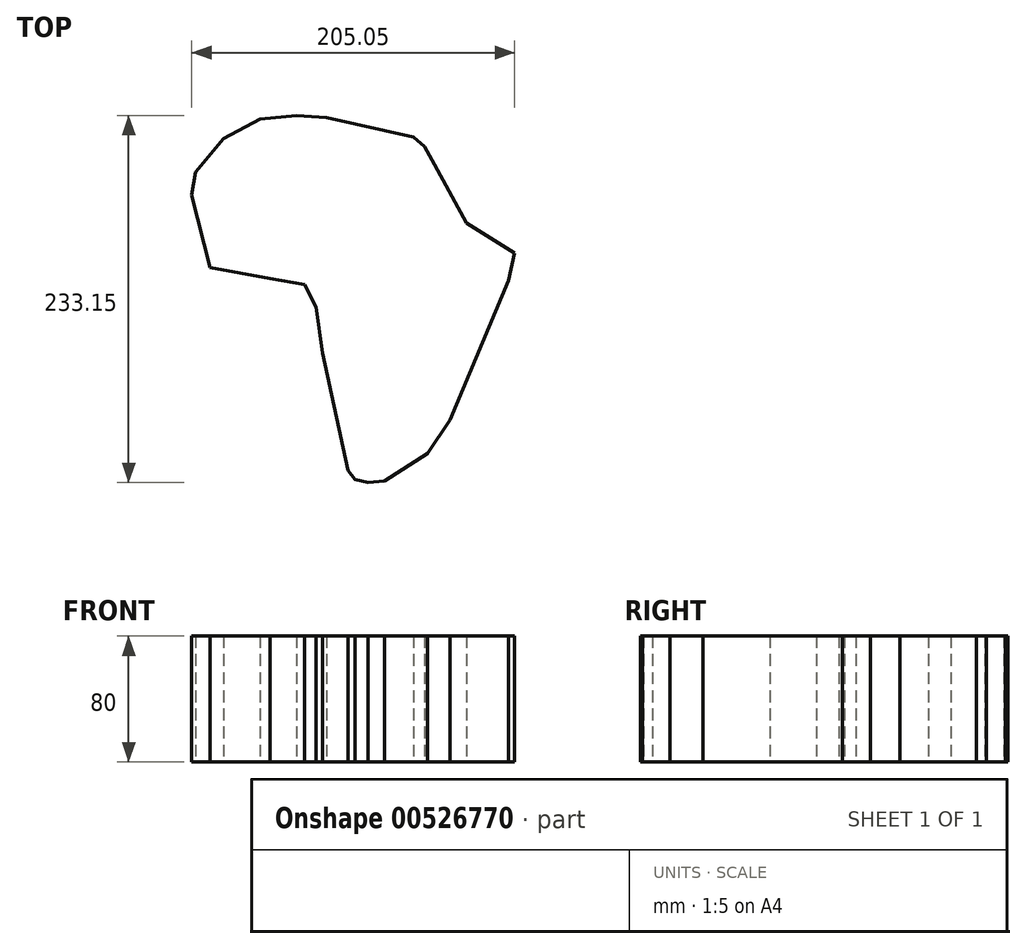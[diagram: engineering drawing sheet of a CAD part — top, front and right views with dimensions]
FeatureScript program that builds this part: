
annotation { "Feature Type Name" : "Feature", "Feature Type Description" : "" }
export const myFeature = defineFeature(function(context is Context, id is Id, definition is map)
    precondition{}
    {
        {
            var Q0;
            Q0=qCreatedBy(makeId("Top.planeOp"),FACE);
            var sketch = newSketch(context, id + "F0", { "sketchPlane" : qUnion([Q0])});
            skLineSegment(sketch, "E0", {"start": v(-465.72, -27.87) * mm, "end": v(-465.72, 203.52) * mm});
            skLineSegment(sketch, "E1", {"start": v(-465.72, 203.52) * mm, "end": v(34.28, 203.52) * mm});
            skLineSegment(sketch, "E2", {"start": v(34.28, 203.52) * mm, "end": v(534.28, 203.52) * mm});
            skLineSegment(sketch, "E3", {"start": v(534.28, 203.52) * mm, "end": v(534.28, -27.87) * mm});
            skLineSegment(sketch, "E4", {"start": v(534.28, -27.87) * mm, "end": v(534.28, -259.27) * mm});
            skLineSegment(sketch, "E5", {"start": v(534.28, -259.27) * mm, "end": v(34.28, -259.27) * mm});
            skLineSegment(sketch, "E6", {"start": v(34.28, -259.27) * mm, "end": v(-465.72, -259.27) * mm});
            skLineSegment(sketch, "E7", {"start": v(-465.72, -259.27) * mm, "end": v(-465.72, -27.87) * mm});
            skLineSegment(sketch, "E8", {"start": v(528.39, -27.87) * mm, "end": v(528.39, 197.62) * mm});
            skLineSegment(sketch, "E9", {"start": v(528.39, 197.62) * mm, "end": v(34.28, 197.62) * mm});
            skLineSegment(sketch, "E10", {"start": v(34.28, 197.62) * mm, "end": v(-459.82, 197.62) * mm});
            skLineSegment(sketch, "E11", {"start": v(-459.82, 197.62) * mm, "end": v(-459.82, -27.87) * mm});
            skLineSegment(sketch, "E12", {"start": v(-459.82, -27.87) * mm, "end": v(-459.82, -253.37) * mm});
            skLineSegment(sketch, "E13", {"start": v(-459.82, -253.37) * mm, "end": v(34.28, -253.37) * mm});
            skLineSegment(sketch, "E14", {"start": v(34.28, -253.37) * mm, "end": v(528.39, -253.37) * mm});
            skLineSegment(sketch, "E15", {"start": v(528.39, -253.37) * mm, "end": v(528.39, -27.87) * mm});
            skLineSegment(sketch, "E16", {"start": v(-215.42, -237.03) * mm, "end": v(-218.6, -212.47) * mm});
            skLineSegment(sketch, "E17", {"start": v(-218.6, -212.47) * mm, "end": v(-201.87, -170.47) * mm});
            skLineSegment(sketch, "E18", {"start": v(-201.87, -170.47) * mm, "end": v(-153.34, -90.03) * mm});
            skLineSegment(sketch, "E19", {"start": v(-153.34, -90.03) * mm, "end": v(-154.95, -75.15) * mm});
            skLineSegment(sketch, "E20", {"start": v(-154.95, -75.15) * mm, "end": v(-201.75, -38.97) * mm});
            skLineSegment(sketch, "E21", {"start": v(-201.75, -38.97) * mm, "end": v(-258.28, -21.52) * mm});
            skLineSegment(sketch, "E22", {"start": v(-258.28, -21.52) * mm, "end": v(-275.6, -23.25) * mm});
            skLineSegment(sketch, "E23", {"start": v(-275.6, -23.25) * mm, "end": v(-281.86, -24.56) * mm});
            skLineSegment(sketch, "E24", {"start": v(-281.86, -24.56) * mm, "end": v(-282.6, -27.58) * mm});
            skLineSegment(sketch, "E25", {"start": v(-282.6, -27.58) * mm, "end": v(-284.13, -31.63) * mm});
            skLineSegment(sketch, "E26", {"start": v(-284.13, -31.63) * mm, "end": v(-297, -64.53) * mm});
            skLineSegment(sketch, "E27", {"start": v(-297, -64.53) * mm, "end": v(-292.56, -86.46) * mm});
            skLineSegment(sketch, "E28", {"start": v(-292.56, -86.46) * mm, "end": v(-273.22, -112.2) * mm});
            skLineSegment(sketch, "E29", {"start": v(-273.22, -112.2) * mm, "end": v(-264.94, -121.42) * mm});
            skLineSegment(sketch, "E30", {"start": v(-264.94, -121.42) * mm, "end": v(-261.57, -146.52) * mm});
            skLineSegment(sketch, "E31", {"start": v(-261.57, -146.52) * mm, "end": v(-248.27, -214.7) * mm});
            skLineSegment(sketch, "E32", {"start": v(-248.27, -214.7) * mm, "end": v(-235.22, -230.35) * mm});
            skLineSegment(sketch, "E33", {"start": v(-235.22, -230.35) * mm, "end": v(-214.64, -241.3) * mm});
            skLineSegment(sketch, "E34", {"start": v(-214.64, -241.3) * mm, "end": v(-215.42, -237.03) * mm});
            skLineSegment(sketch, "E35", {"start": v(-215.42, -237.03) * mm, "end": v(-215.42, -237.03) * mm});
            skLineSegment(sketch, "E36", {"start": v(-293.37, -30.58) * mm, "end": v(-289.65, -28.13) * mm});
            skLineSegment(sketch, "E37", {"start": v(-289.65, -28.13) * mm, "end": v(-293.12, -24.82) * mm});
            skLineSegment(sketch, "E38", {"start": v(-293.12, -24.82) * mm, "end": v(-305, -14.19) * mm});
            skLineSegment(sketch, "E39", {"start": v(-305, -14.19) * mm, "end": v(-321.94, 24.08) * mm});
            skLineSegment(sketch, "E40", {"start": v(-321.94, 24.08) * mm, "end": v(-298.96, 37.24) * mm});
            skLineSegment(sketch, "E41", {"start": v(-298.96, 37.24) * mm, "end": v(-262.72, 60.23) * mm});
            skLineSegment(sketch, "E42", {"start": v(-262.72, 60.23) * mm, "end": v(-214.85, 92.1) * mm});
            skLineSegment(sketch, "E43", {"start": v(-214.85, 92.1) * mm, "end": v(-194.9, 105.1) * mm});
            skLineSegment(sketch, "E44", {"start": v(-194.9, 105.1) * mm, "end": v(-185.9, 127.77) * mm});
            skLineSegment(sketch, "E45", {"start": v(-185.9, 127.77) * mm, "end": v(-201.02, 144.52) * mm});
            skLineSegment(sketch, "E46", {"start": v(-201.02, 144.52) * mm, "end": v(-237.27, 166.66) * mm});
            skLineSegment(sketch, "E47", {"start": v(-237.27, 166.66) * mm, "end": v(-255.45, 170.7) * mm});
            skLineSegment(sketch, "E48", {"start": v(-255.45, 170.7) * mm, "end": v(-262.2, 172.5) * mm});
            skLineSegment(sketch, "E49", {"start": v(-262.2, 172.5) * mm, "end": v(-273.5, 171.12) * mm});
            skLineSegment(sketch, "E50", {"start": v(-273.5, 171.12) * mm, "end": v(-357.4, 168.14) * mm});
            skLineSegment(sketch, "E51", {"start": v(-357.4, 168.14) * mm, "end": v(-402.57, 164.46) * mm});
            skLineSegment(sketch, "E52", {"start": v(-402.57, 164.46) * mm, "end": v(-436.03, 150.53) * mm});
            skLineSegment(sketch, "E53", {"start": v(-436.03, 150.53) * mm, "end": v(-444.1, 129.4) * mm});
            skLineSegment(sketch, "E54", {"start": v(-444.1, 129.4) * mm, "end": v(-443.17, 126.41) * mm});
            skLineSegment(sketch, "E55", {"start": v(-443.17, 126.41) * mm, "end": v(-394.54, 129.69) * mm});
            skLineSegment(sketch, "E56", {"start": v(-394.54, 129.69) * mm, "end": v(-390.53, 123.1) * mm});
            skLineSegment(sketch, "E57", {"start": v(-390.53, 123.1) * mm, "end": v(-399.09, 94.9) * mm});
            skLineSegment(sketch, "E58", {"start": v(-399.09, 94.9) * mm, "end": v(-404.83, 69.28) * mm});
            skLineSegment(sketch, "E59", {"start": v(-404.83, 69.28) * mm, "end": v(-360.81, -1.67) * mm});
            skLineSegment(sketch, "E60", {"start": v(-360.81, -1.67) * mm, "end": v(-352.97, -4.65) * mm});
            skLineSegment(sketch, "E61", {"start": v(-352.97, -4.65) * mm, "end": v(-319.44, -20.87) * mm});
            skLineSegment(sketch, "E62", {"start": v(-319.44, -20.87) * mm, "end": v(-297.36, -33.03) * mm});
            skLineSegment(sketch, "E63", {"start": v(-297.36, -33.03) * mm, "end": v(-293.37, -30.58) * mm});
            skLineSegment(sketch, "E64", {"start": v(-293.37, -30.58) * mm, "end": v(-293.37, -30.58) * mm});
            skLineSegment(sketch, "E65", {"start": v(354.76, -204.8) * mm, "end": v(354.76, -204.8) * mm});
            skLineSegment(sketch, "E66", {"start": v(367.47, -196.96) * mm, "end": v(409, -155.32) * mm});
            skLineSegment(sketch, "E67", {"start": v(409, -155.32) * mm, "end": v(394.17, -109.22) * mm});
            skLineSegment(sketch, "E68", {"start": v(394.17, -109.22) * mm, "end": v(370.77, -99.72) * mm});
            skLineSegment(sketch, "E69", {"start": v(370.77, -99.72) * mm, "end": v(354.02, -99.72) * mm});
            skLineSegment(sketch, "E70", {"start": v(354.02, -99.72) * mm, "end": v(345.59, -106.08) * mm});
            skLineSegment(sketch, "E71", {"start": v(345.59, -106.08) * mm, "end": v(319.84, -123.28) * mm});
            skLineSegment(sketch, "E72", {"start": v(319.84, -123.28) * mm, "end": v(305.7, -128.37) * mm});
            skLineSegment(sketch, "E73", {"start": v(305.7, -128.37) * mm, "end": v(292.54, -133.76) * mm});
            skLineSegment(sketch, "E74", {"start": v(292.54, -133.76) * mm, "end": v(290.2, -135.73) * mm});
            skLineSegment(sketch, "E75", {"start": v(290.2, -135.73) * mm, "end": v(290.72, -146.92) * mm});
            skLineSegment(sketch, "E76", {"start": v(290.72, -146.92) * mm, "end": v(290.37, -162.45) * mm});
            skLineSegment(sketch, "E77", {"start": v(290.37, -162.45) * mm, "end": v(284.64, -173.75) * mm});
            skLineSegment(sketch, "E78", {"start": v(284.64, -173.75) * mm, "end": v(304.73, -169.36) * mm});
            skLineSegment(sketch, "E79", {"start": v(304.73, -169.36) * mm, "end": v(328.19, -164.46) * mm});
            skLineSegment(sketch, "E80", {"start": v(328.19, -164.46) * mm, "end": v(350.99, -186.68) * mm});
            skLineSegment(sketch, "E81", {"start": v(350.99, -186.68) * mm, "end": v(356, -198) * mm});
            skLineSegment(sketch, "E82", {"start": v(356, -198) * mm, "end": v(360.09, -200.07) * mm});
            skLineSegment(sketch, "E83", {"start": v(360.09, -200.07) * mm, "end": v(367.47, -196.96) * mm});
            skLineSegment(sketch, "E84", {"start": v(367.47, -196.96) * mm, "end": v(367.47, -196.96) * mm});
            skLineSegment(sketch, "E85", {"start": v(1.41, -178.26) * mm, "end": v(1.41, -178.26) * mm});
            skLineSegment(sketch, "E86", {"start": v(20.87, -172.69) * mm, "end": v(48.35, -155.21) * mm});
            skLineSegment(sketch, "E87", {"start": v(48.35, -155.21) * mm, "end": v(62.69, -134.08) * mm});
            skLineSegment(sketch, "E88", {"start": v(62.69, -134.08) * mm, "end": v(99.7, -45.56) * mm});
            skLineSegment(sketch, "E89", {"start": v(99.7, -45.56) * mm, "end": v(103.64, -27.87) * mm});
            skLineSegment(sketch, "E90", {"start": v(103.64, -27.87) * mm, "end": v(73.21, -9.08) * mm});
            skLineSegment(sketch, "E91", {"start": v(73.21, -9.08) * mm, "end": v(52.72, 28.1) * mm});
            skLineSegment(sketch, "E92", {"start": v(52.72, 28.1) * mm, "end": v(46.32, 39.66) * mm});
            skLineSegment(sketch, "E93", {"start": v(46.32, 39.66) * mm, "end": v(39.48, 45.74) * mm});
            skLineSegment(sketch, "E94", {"start": v(39.48, 45.74) * mm, "end": v(-15.83, 58.1) * mm});
            skLineSegment(sketch, "E95", {"start": v(-15.83, 58.1) * mm, "end": v(-34.99, 59.37) * mm});
            skLineSegment(sketch, "E96", {"start": v(-34.99, 59.37) * mm, "end": v(-58.1, 57.05) * mm});
            skLineSegment(sketch, "E97", {"start": v(-58.1, 57.05) * mm, "end": v(-81.33, 44.78) * mm});
            skLineSegment(sketch, "E98", {"start": v(-81.33, 44.78) * mm, "end": v(-98.85, 23.3) * mm});
            skLineSegment(sketch, "E99", {"start": v(-98.85, 23.3) * mm, "end": v(-101.4, 8.94) * mm});
            skLineSegment(sketch, "E100", {"start": v(-101.4, 8.94) * mm, "end": v(-89.78, -37.1) * mm});
            skLineSegment(sketch, "E101", {"start": v(-89.78, -37.1) * mm, "end": v(-51.81, -44.31) * mm});
            skLineSegment(sketch, "E102", {"start": v(-51.81, -44.31) * mm, "end": v(-29.88, -47.92) * mm});
            skLineSegment(sketch, "E103", {"start": v(-29.88, -47.92) * mm, "end": v(-22.6, -62.14) * mm});
            skLineSegment(sketch, "E104", {"start": v(-22.6, -62.14) * mm, "end": v(-18.4, -91.62) * mm});
            skLineSegment(sketch, "E105", {"start": v(-18.4, -91.62) * mm, "end": v(-2.16, -166.12) * mm});
            skLineSegment(sketch, "E106", {"start": v(-2.16, -166.12) * mm, "end": v(2.31, -171.9) * mm});
            skLineSegment(sketch, "E107", {"start": v(2.31, -171.9) * mm, "end": v(10.6, -173.78) * mm});
            skLineSegment(sketch, "E108", {"start": v(10.6, -173.78) * mm, "end": v(20.87, -172.69) * mm});
            skLineSegment(sketch, "E109", {"start": v(189.02, -26.58) * mm, "end": v(192.1, -17.98) * mm});
            skLineSegment(sketch, "E110", {"start": v(192.1, -17.98) * mm, "end": v(222.01, 17.04) * mm});
            skLineSegment(sketch, "E111", {"start": v(222.01, 17.04) * mm, "end": v(238.71, -4.3) * mm});
            skLineSegment(sketch, "E112", {"start": v(238.71, -4.3) * mm, "end": v(253.04, -23.46) * mm});
            skLineSegment(sketch, "E113", {"start": v(253.04, -23.46) * mm, "end": v(276.96, -22.34) * mm});
            skLineSegment(sketch, "E114", {"start": v(276.96, -22.34) * mm, "end": v(292.98, 5.52) * mm});
            skLineSegment(sketch, "E115", {"start": v(292.98, 5.52) * mm, "end": v(303.31, 34.5) * mm});
            skLineSegment(sketch, "E116", {"start": v(303.31, 34.5) * mm, "end": v(328.31, 48.44) * mm});
            skLineSegment(sketch, "E117", {"start": v(328.31, 48.44) * mm, "end": v(354.47, 64.54) * mm});
            skLineSegment(sketch, "E118", {"start": v(354.47, 64.54) * mm, "end": v(345.27, 81.2) * mm});
            skLineSegment(sketch, "E119", {"start": v(345.27, 81.2) * mm, "end": v(337.37, 97.55) * mm});
            skLineSegment(sketch, "E120", {"start": v(337.37, 97.55) * mm, "end": v(357.42, 113.24) * mm});
            skLineSegment(sketch, "E121", {"start": v(357.42, 113.24) * mm, "end": v(369.6, 122.18) * mm});
            skLineSegment(sketch, "E122", {"start": v(369.6, 122.18) * mm, "end": v(383.56, 139.36) * mm});
            skLineSegment(sketch, "E123", {"start": v(383.56, 139.36) * mm, "end": v(395, 151.78) * mm});
            skLineSegment(sketch, "E124", {"start": v(395, 151.78) * mm, "end": v(361.3, 160.43) * mm});
            skLineSegment(sketch, "E125", {"start": v(361.3, 160.43) * mm, "end": v(180.56, 184.11) * mm});
            skLineSegment(sketch, "E126", {"start": v(180.56, 184.11) * mm, "end": v(156.24, 181.9) * mm});
            skLineSegment(sketch, "E127", {"start": v(156.24, 181.9) * mm, "end": v(72.84, 161.62) * mm});
            skLineSegment(sketch, "E128", {"start": v(72.84, 161.62) * mm, "end": v(78.52, 127.26) * mm});
            skLineSegment(sketch, "E129", {"start": v(78.52, 127.26) * mm, "end": v(84.27, 91.65) * mm});
            skLineSegment(sketch, "E130", {"start": v(84.27, 91.65) * mm, "end": v(71.83, 70.15) * mm});
            skLineSegment(sketch, "E131", {"start": v(71.83, 70.15) * mm, "end": v(59.02, 48.86) * mm});
            skLineSegment(sketch, "E132", {"start": v(59.02, 48.86) * mm, "end": v(66.67, 29.6) * mm});
            skLineSegment(sketch, "E133", {"start": v(66.67, 29.6) * mm, "end": v(85.84, -7.13) * mm});
            skLineSegment(sketch, "E134", {"start": v(85.84, -7.13) * mm, "end": v(93.82, -5.06) * mm});
            skLineSegment(sketch, "E135", {"start": v(93.82, -5.06) * mm, "end": v(124.18, 15.94) * mm});
            skLineSegment(sketch, "E136", {"start": v(124.18, 15.94) * mm, "end": v(132.9, 23.96) * mm});
            skLineSegment(sketch, "E137", {"start": v(132.9, 23.96) * mm, "end": v(165.9, 14.28) * mm});
            skLineSegment(sketch, "E138", {"start": v(165.9, 14.28) * mm, "end": v(172.45, 7.45) * mm});
            skLineSegment(sketch, "E139", {"start": v(172.45, 7.45) * mm, "end": v(179.22, -16.93) * mm});
            skLineSegment(sketch, "E140", {"start": v(179.22, -16.93) * mm, "end": v(189.02, -26.58) * mm});
            skLineSegment(sketch, "E141", {"start": v(189.02, -26.58) * mm, "end": v(189.02, -26.58) * mm});
            skLineSegment(sketch, "E142", {"start": v(55.96, 64.7) * mm, "end": v(70.84, 85.8) * mm});
            skLineSegment(sketch, "E143", {"start": v(70.84, 85.8) * mm, "end": v(72.53, 89.3) * mm});
            skLineSegment(sketch, "E144", {"start": v(72.53, 89.3) * mm, "end": v(71.25, 97.22) * mm});
            skLineSegment(sketch, "E145", {"start": v(71.25, 97.22) * mm, "end": v(64.7, 133.03) * mm});
            skLineSegment(sketch, "E146", {"start": v(64.7, 133.03) * mm, "end": v(57.9, 161.5) * mm});
            skLineSegment(sketch, "E147", {"start": v(57.9, 161.5) * mm, "end": v(14.91, 165.84) * mm});
            skLineSegment(sketch, "E148", {"start": v(14.91, 165.84) * mm, "end": v(1.44, 166.3) * mm});
            skLineSegment(sketch, "E149", {"start": v(1.44, 166.3) * mm, "end": v(-2.27, 161.73) * mm});
            skLineSegment(sketch, "E150", {"start": v(-2.27, 161.73) * mm, "end": v(-18.6, 146.91) * mm});
            skLineSegment(sketch, "E151", {"start": v(-18.6, 146.91) * mm, "end": v(-20.56, 134.57) * mm});
            skLineSegment(sketch, "E152", {"start": v(-20.56, 134.57) * mm, "end": v(-33.14, 125.04) * mm});
            skLineSegment(sketch, "E153", {"start": v(-33.14, 125.04) * mm, "end": v(-46.6, 124.14) * mm});
            skLineSegment(sketch, "E154", {"start": v(-46.6, 124.14) * mm, "end": v(-53.07, 129.83) * mm});
            skLineSegment(sketch, "E155", {"start": v(-53.07, 129.83) * mm, "end": v(-60.36, 126.01) * mm});
            skLineSegment(sketch, "E156", {"start": v(-60.36, 126.01) * mm, "end": v(-72.2, 116.7) * mm});
            skLineSegment(sketch, "E157", {"start": v(-72.2, 116.7) * mm, "end": v(-60.9, 100.61) * mm});
            skLineSegment(sketch, "E158", {"start": v(-60.9, 100.61) * mm, "end": v(-61.76, 87.79) * mm});
            skLineSegment(sketch, "E159", {"start": v(-61.76, 87.79) * mm, "end": v(-70.32, 86.27) * mm});
            skLineSegment(sketch, "E160", {"start": v(-70.32, 86.27) * mm, "end": v(-72.94, 70.61) * mm});
            skLineSegment(sketch, "E161", {"start": v(-72.94, 70.61) * mm, "end": v(-72.94, 66.58) * mm});
            skLineSegment(sketch, "E162", {"start": v(-72.94, 66.58) * mm, "end": v(-69.95, 66.08) * mm});
            skLineSegment(sketch, "E163", {"start": v(-69.95, 66.08) * mm, "end": v(-52.14, 67.27) * mm});
            skLineSegment(sketch, "E164", {"start": v(-52.14, 67.27) * mm, "end": v(-43.85, 74.93) * mm});
            skLineSegment(sketch, "E165", {"start": v(-43.85, 74.93) * mm, "end": v(-22.65, 89.01) * mm});
            skLineSegment(sketch, "E166", {"start": v(-22.65, 89.01) * mm, "end": v(-12.82, 81.28) * mm});
            skLineSegment(sketch, "E167", {"start": v(-12.82, 81.28) * mm, "end": v(-2.46, 72.47) * mm});
            skLineSegment(sketch, "E168", {"start": v(-2.46, 72.47) * mm, "end": v(45.7, 59.62) * mm});
            skLineSegment(sketch, "E169", {"start": v(45.7, 59.62) * mm, "end": v(55.96, 64.7) * mm});
            skLineSegment(sketch, "E170", {"start": v(55.96, 64.7) * mm, "end": v(55.96, 64.7) * mm});
            skSolve(sketch);
        }
        {
            var Q0;
            Q0=makeQuery(id+"F0.imprint","IMPRINT",FACE,{"disambiguationData":[TD([[makeQuery(id+"F0.imprint","IMPRINT",EDGE,{"derivedFrom":sQuery(id+"F0.wireOp",EDGE,"E86")}),1.0]])]});
            extrude(context, id + "F1", {"entities" : qUnion([Q0]), "depth" : 80 * mm, "offsetDistance" : 25 * mm});
        }
    });
